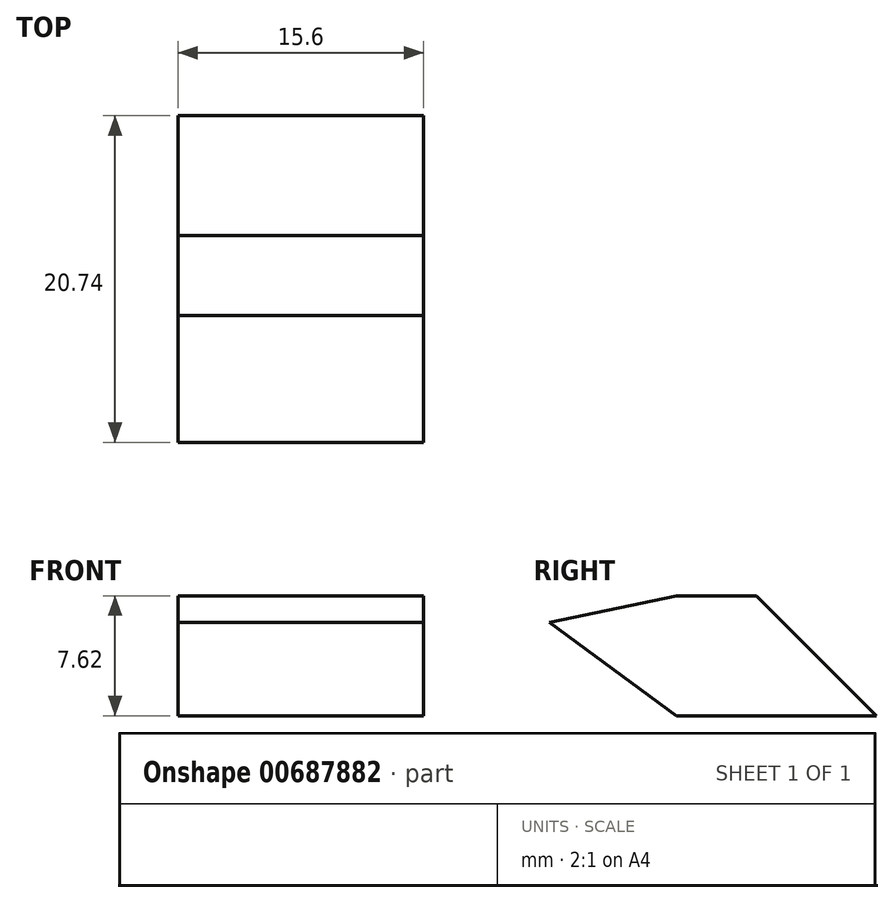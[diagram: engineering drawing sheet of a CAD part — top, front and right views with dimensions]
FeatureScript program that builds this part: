
annotation { "Feature Type Name" : "Feature", "Feature Type Description" : "" }
export const myFeature = defineFeature(function(context is Context, id is Id, definition is map)
    precondition{}
    {
        {
            var Q0;
            Q0=qCreatedBy(makeId("Right.planeOp"),FACE);
            var sketch = newSketch(context, id + "F0", { "sketchPlane" : qUnion([Q0])});
            skLineSegment(sketch, "E0.bottom", {"start": v(0, 0) * mm, "end": v(-12.7, 0) * mm});
            skLineSegment(sketch, "E0.top", {"start": v(0, 7.62) * mm, "end": v(-12.7, 7.62) * mm});
            skLineSegment(sketch, "E0.left", {"start": v(0, 0) * mm, "end": v(0, 7.62) * mm});
            skLineSegment(sketch, "E0.right", {"start": v(-12.7, 0) * mm, "end": v(-12.7, 7.62) * mm});
            skLineSegment(sketch, "E1", {"start": v(-12.7, 0) * mm, "end": v(-20.74, 5.93) * mm});
            skLineSegment(sketch, "E2", {"start": v(-20.74, 5.93) * mm, "end": v(-12.7, 7.62) * mm});
            skSolve(sketch);
        }
        {
            var Q0;
            Q0 = qSketchRegion(id + "F0", true);
            extrude(context, id + "F1", {"entities" : qUnion([Q0]), "depth" : 15.6 * mm, "offsetDistance" : 25.4 * mm});
        }
        {
            var Q0;
            Q0=makeQuery(id+"F1.opExtrude","SWEPT_EDGE",EDGE,{"disambiguationData":[OSD([sQuery(id+"F0.wireOp",EDGE,"E0.top"),sQuery(id+"F0.wireOp",EDGE,"E0.left")])]});
            chamfer(context, id + "F2", {"entities" : qUnion([Q0]), "width" : 7.62 * mm, "tangentPropagation" : true});
        }
    });
